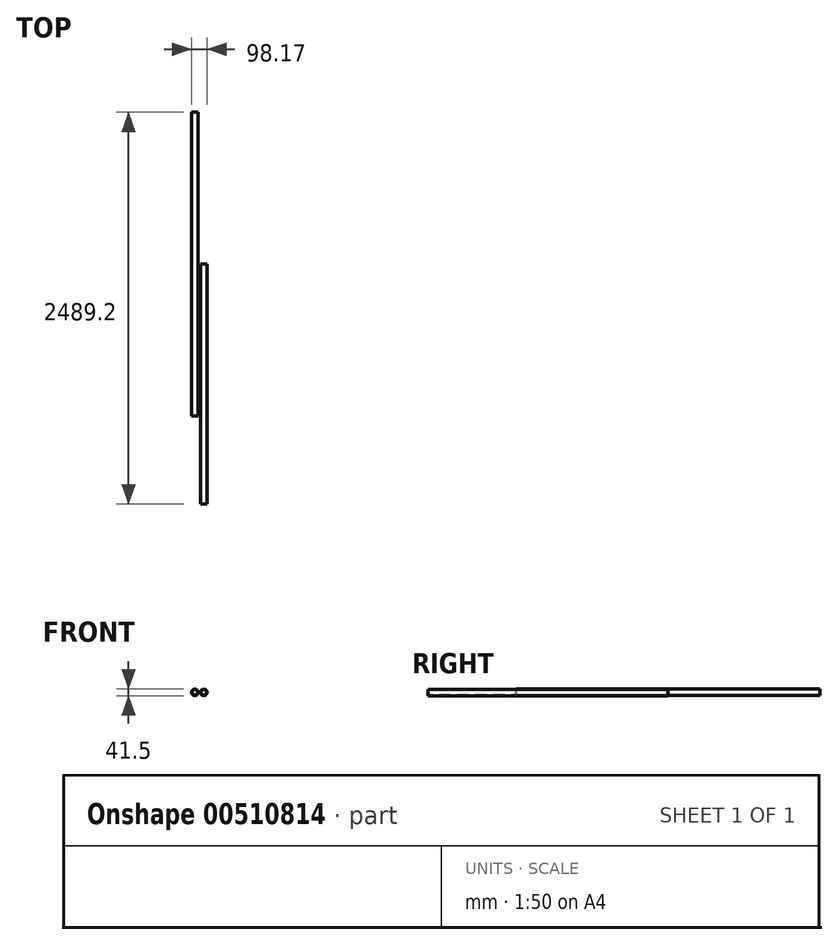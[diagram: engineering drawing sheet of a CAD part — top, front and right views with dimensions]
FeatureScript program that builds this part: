
annotation { "Feature Type Name" : "Feature", "Feature Type Description" : "" }
export const myFeature = defineFeature(function(context is Context, id is Id, definition is map)
    precondition{}
    {
        {
            var Q0;
            Q0=qCreatedBy(makeId("Front.planeOp"),FACE);
            var sketch = newSketch(context, id + "F0", { "sketchPlane" : qUnion([Q0])});
            skCircle(sketch, "E0", {"center": v(-54.17, 7.93) * mm, "radius": 20.64 * mm});
            skCircle(sketch, "E1", {"center": v(-54.17, 7.93) * mm, "radius": 17.46 * mm});
            skSolve(sketch);
        }
        {
            var Q0;
            Q0=sQuery(id+"F0.wireOp",EDGE,"E0");
            var Q1;
            Q1=sQuery(id+"F0.wireOp",EDGE,"E1");
            extrude(context, id + "F1", {"bodyType" : ToolBodyType.SURFACE, "surfaceEntities" : qUnion([Q0, Q1]), "endBound" : BoundingType.SYMMETRIC, "depth" : 1930.4 * mm});
        }
        {
            var Q0;
            Q0=qCreatedBy(makeId("Front.planeOp"),FACE);
            var sketch = newSketch(context, id + "F2", { "sketchPlane" : qUnion([Q0])});
            skCircle(sketch, "E2", {"center": v(2.72, 7.7) * mm, "radius": 20.64 * mm});
            skCircle(sketch, "E3", {"center": v(2.72, 7.95) * mm, "radius": 17.46 * mm});
            skSolve(sketch);
        }
        {
            var Q0;
            Q0=sQuery(id+"F2.wireOp",EDGE,"E3");
            var Q1;
            Q1=sQuery(id+"F2.wireOp",EDGE,"E2");
            extrude(context, id + "F3", {"bodyType" : ToolBodyType.SURFACE, "surfaceEntities" : qUnion([Q0, Q1]), "depth" : 1524 * mm});
        }
    });
